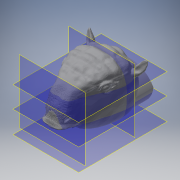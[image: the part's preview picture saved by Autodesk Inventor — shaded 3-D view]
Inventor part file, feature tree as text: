
AUTODESK INVENTOR PART (.ipt)
format: ipt  version: 2019 (Build 230136000, 136)  size: 18,918,912 bytes
history: native  units: in
note: dims shown in document units (in); Inventor stores cm internally (conversion verified against a paired STEP export)
features: other x6, sketch x6, reference x6, plane x5, extrude x3, loft x1
ambient origin geometry x8: Origin, YZ Plane, XZ Plane, XY Plane, X Axis, Y Axis, Z Axis, Center Point
bodies: Solid1 (feature_tree)
feature tree (27):
  other  "Glyptodon Reduced 3.ipt"
  plane  "Work Plane1"
  sketch  "Sketch1"  dims[d0=0.0077in d1=3.5in]
  plane  "Work Plane2"
  extrude  "Extrusion1"  Depth=3.5in
  extrude  "Extrusion2"  Depth=0.1in
  extrude  "Extrusion3"  Depth=3.5in TaperAngle=0.0deg
  plane  "Work Plane3"
  sketch  "Sketch4"  dims[d11=90.0deg d12=2.1in]
  plane  "Work Plane5"
  loft  "Loft1"
  other  "Solid1::Glyptodon Reduced 3.ipt"
  other  "TaggingFeature1"
  reference  "Reference1"
  reference  "Reference2"
  reference  "Reference3"
  reference  "Reference4"
  reference  "Reference5"
  reference  "Reference6"
  sketch  "Sketch2"  dims[d2=2.0in d3=0.0in d4=0.1in]
  sketch  "Sketch3"  dims[d5=2.7in d6=0.0in d7=3.5in d8=2.0in d9=0.0in d10=0.0in]
  other  "Work Axis1"
  plane  "Work Plane4"
  sketch  "Sketch5"  dims[d13=2.1in]
  sketch  "Sketch6"  dims[d14=-1.5625in d15=-1.5in d16=0.0in d17=90.0deg d18=0.0in d19=90.0deg d20=0.0in d21=90.0deg]
  other  "Assembly2"
  other  "temp2:1"
